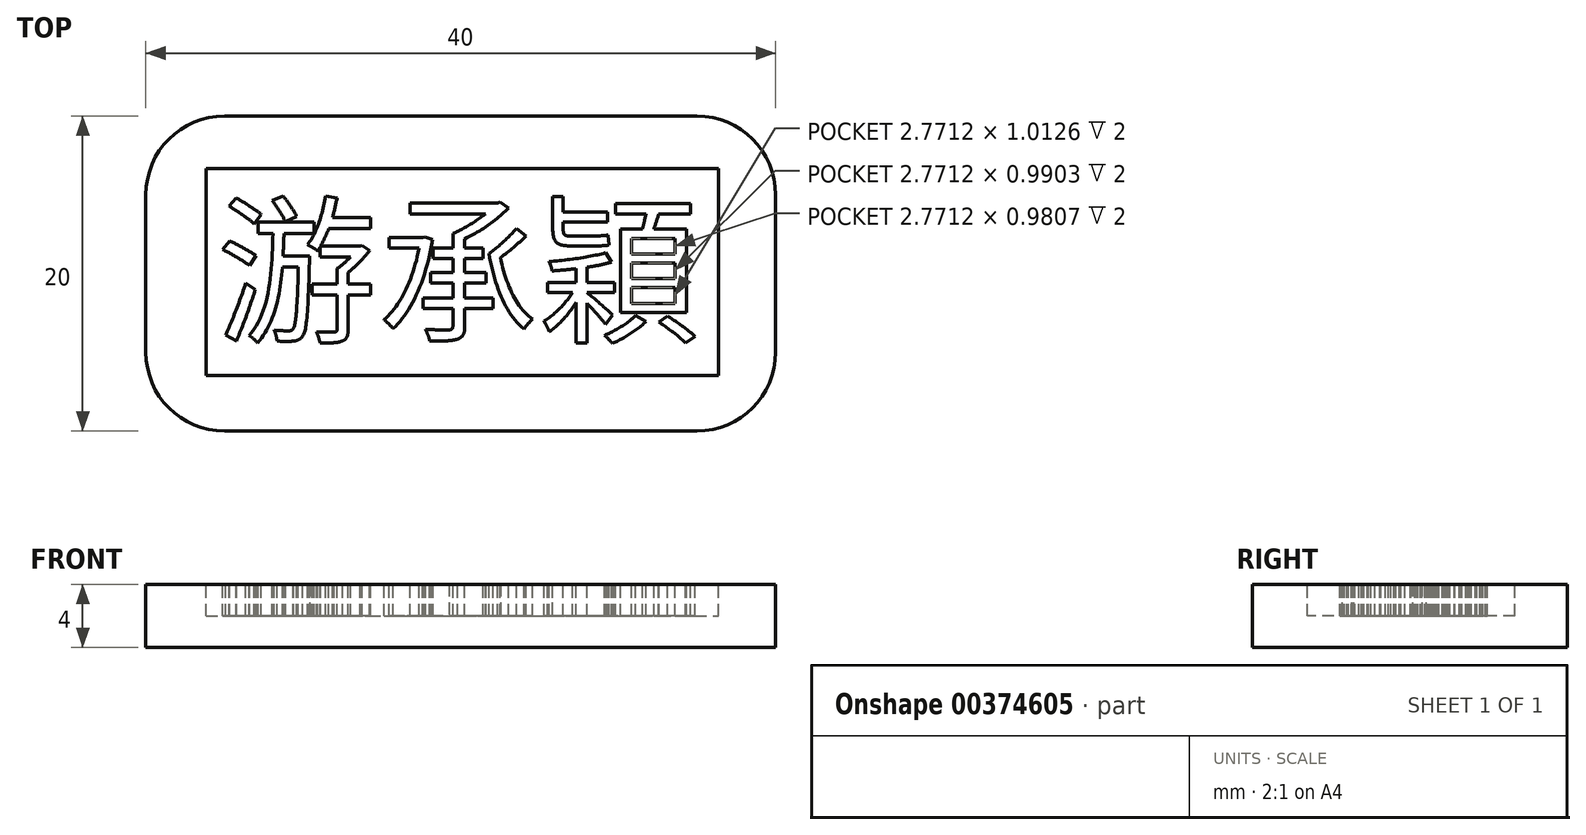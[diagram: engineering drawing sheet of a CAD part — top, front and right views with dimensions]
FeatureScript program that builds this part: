
annotation { "Feature Type Name" : "Feature", "Feature Type Description" : "" }
export const myFeature = defineFeature(function(context is Context, id is Id, definition is map)
    precondition{}
    {
        {
            var Q0;
            Q0=qCreatedBy(makeId("Top.planeOp"),FACE);
            var sketch = newSketch(context, id + "F0", { "sketchPlane" : qUnion([Q0])});
            skLineSegment(sketch, "E0.bottom", {"start": v(-15, 10) * mm, "end": v(15, 10) * mm});
            skLineSegment(sketch, "E0.top", {"start": v(-15, -10) * mm, "end": v(15, -10) * mm});
            skLineSegment(sketch, "E0.left", {"start": v(-20, 5) * mm, "end": v(-20, -5) * mm});
            skLineSegment(sketch, "E0.right", {"start": v(20, 5) * mm, "end": v(20, -5) * mm});
            skPoint(sketch, "E0.middle", {"position": v(0, 0) * mm});
            skPoint(sketch, "E1.visualSharp", {"position": v(-20, 10) * mm});
            skArc(sketch, "E1.filletArc", {"start": v(-15, 10) * mm, "mid": v(-18.54, 8.54) * mm, "end": v(-20, 5) * mm});
            skPoint(sketch, "E2.visualSharp", {"position": v(20, 10) * mm});
            skArc(sketch, "E2.filletArc", {"start": v(20, 5) * mm, "mid": v(18.54, 8.54) * mm, "end": v(15, 10) * mm});
            skPoint(sketch, "E3.visualSharp", {"position": v(20, -10) * mm});
            skArc(sketch, "E3.filletArc", {"start": v(15, -10) * mm, "mid": v(18.54, -8.54) * mm, "end": v(20, -5) * mm});
            skPoint(sketch, "E4.visualSharp", {"position": v(-20, -10) * mm});
            skArc(sketch, "E4.filletArc", {"start": v(-20, -5) * mm, "mid": v(-18.54, -8.54) * mm, "end": v(-15, -10) * mm});
            skSolve(sketch);
        }
        {
            var Q0;
            Q0=makeQuery(id+"F0.imprint","IMPRINT",FACE,{"disambiguationData":[TD([[makeQuery(id+"F0.imprint","IMPRINT",EDGE,{"derivedFrom":sQuery(id+"F0.wireOp",EDGE,"E0.bottom")}),-1.0]])]});
            extrude(context, id + "F1", {"entities" : qUnion([Q0]), "depth" : 4 * mm});
        }
        {
            var Q0;
            Q0=makeQuery(id+"F1.opExtrude","CAP_FACE",FACE,{"disambiguationData":[OSD([sQuery(id+"F0.wireOp",EDGE,"E0.bottom"),sQuery(id+"F0.wireOp",EDGE,"E0.top"),sQuery(id+"F0.wireOp",EDGE,"E0.left"),sQuery(id+"F0.wireOp",EDGE,"E0.right"),sQuery(id+"F0.wireOp",EDGE,"E1.filletArc"),sQuery(id+"F0.wireOp",EDGE,"E2.filletArc"),sQuery(id+"F0.wireOp",EDGE,"E3.filletArc"),sQuery(id+"F0.wireOp",EDGE,"E4.filletArc")])],"isStart":false});
            var sketch = newSketch(context, id + "F2", { "sketchPlane" : qUnion([Q0])});
            skLineSegment(sketch, "E5.bottom", {"start": v(-16.18, 6.68) * mm, "end": v(16.37, 6.68) * mm});
            skLineSegment(sketch, "E5.top", {"start": v(-16.18, -6.5) * mm, "end": v(16.37, -6.5) * mm});
            skLineSegment(sketch, "E5.left", {"start": v(-16.18, 6.68) * mm, "end": v(-16.18, -6.5) * mm});
            skLineSegment(sketch, "E5.right", {"start": v(16.37, 6.68) * mm, "end": v(16.37, -6.5) * mm});
            skText(sketch, "E6", { "text": "游承穎", "fontName": "NotoSansCJKtc-Regular.otf"});
            const initialGuessF2  = {"E6": [-0.01553, -0.00363, 1, 0, 0.00736]};
            skSetInitialGuess(sketch, initialGuessF2);
            skSolve(sketch);
        }
        {
            var Q0;
            Q0=makeQuery(id+"F2.imprint","IMPRINT",FACE,{"disambiguationData":[TD([[makeQuery(id+"F2.imprint","IMPRINT",EDGE,{"derivedFrom":sQuery(id+"F2.wireOp",EDGE,"E5.bottom")}),-1.0]])]});
            var Q1;
            Q1=makeQuery(id+"F2.imprint","IMPRINT",FACE,{"disambiguationData":[TD([[makeQuery(id+"F2.imprint","IMPRINT",EDGE,{"derivedFrom":sQuery(id+"F2.wireOp",EDGE,"9c631159-2112-45b8-b234-8aa999b55fa5.sketch_text.stroke-22")}),-1.0]])]});
            var Q2;
            Q2=makeQuery(id+"F2.imprint","IMPRINT",FACE,{"disambiguationData":[TD([[makeQuery(id+"F2.imprint","IMPRINT",EDGE,{"derivedFrom":sQuery(id+"F2.wireOp",EDGE,"9c631159-2112-45b8-b234-8aa999b55fa5.sketch_text.stroke-49")}),-1.0]])]});
            var Q3;
            Q3=makeQuery(id+"F2.imprint","IMPRINT",FACE,{"disambiguationData":[TD([[makeQuery(id+"F2.imprint","IMPRINT",EDGE,{"derivedFrom":sQuery(id+"F2.wireOp",EDGE,"E6.sketch_text.stroke-126")}),-1.0]])]});
            var Q4;
            Q4=makeQuery(id+"F2.imprint","IMPRINT",FACE,{"disambiguationData":[TD([[makeQuery(id+"F2.imprint","IMPRINT",EDGE,{"derivedFrom":sQuery(id+"F2.wireOp",EDGE,"E6.sketch_text.stroke-122")}),-1.0]])]});
            var Q5;
            Q5=makeQuery(id+"F2.imprint","IMPRINT",FACE,{"disambiguationData":[TD([[makeQuery(id+"F2.imprint","IMPRINT",EDGE,{"derivedFrom":sQuery(id+"F2.wireOp",EDGE,"E6.sketch_text.stroke-118")}),-1.0]])]});
            extrude(context, id + "F3", {"entities" : qUnion([Q0, Q1, Q2, Q3, Q4, Q5]), "operationType" : NewBodyOperationType.REMOVE, "oppositeDirection" : true, "depth" : 2 * mm});
        }
    });
